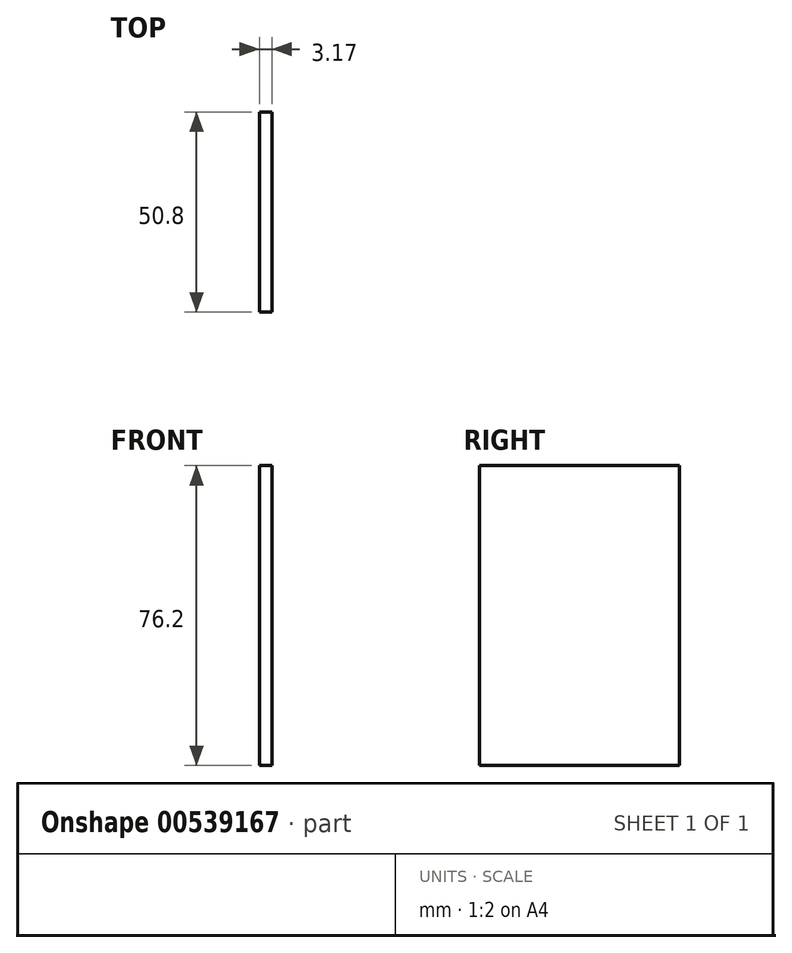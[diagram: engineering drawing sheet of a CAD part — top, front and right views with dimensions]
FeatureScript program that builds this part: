
annotation { "Feature Type Name" : "Feature", "Feature Type Description" : "" }
export const myFeature = defineFeature(function(context is Context, id is Id, definition is map)
    precondition{}
    {
        {
            var Q0;
            Q0=qCreatedBy(makeId("Right.planeOp"),FACE);
            var sketch = newSketch(context, id + "F0", { "sketchPlane" : qUnion([Q0])});
            skLineSegment(sketch, "E0.bottom", {"start": v(-25.4, -38.1) * mm, "end": v(25.4, -38.1) * mm});
            skLineSegment(sketch, "E0.top", {"start": v(-25.4, 38.1) * mm, "end": v(25.4, 38.1) * mm});
            skLineSegment(sketch, "E0.left", {"start": v(-25.4, -38.1) * mm, "end": v(-25.4, 38.1) * mm});
            skLineSegment(sketch, "E0.right", {"start": v(25.4, -38.1) * mm, "end": v(25.4, 38.1) * mm});
            skPoint(sketch, "E0.middle", {"position": v(0, 0) * mm});
            skSolve(sketch);
        }
        {
            var Q0;
            Q0=makeQuery(id+"F0.imprint","IMPRINT",FACE,{"disambiguationData":[TD([[makeQuery(id+"F0.imprint","IMPRINT",EDGE,{"derivedFrom":sQuery(id+"F0.wireOp",EDGE,"E0.bottom")}),1.0]])]});
            extrude(context, id + "F1", {"entities" : qUnion([Q0]), "depth" : 3.17 * mm, "offsetDistance" : 25.4 * mm});
        }
    });
